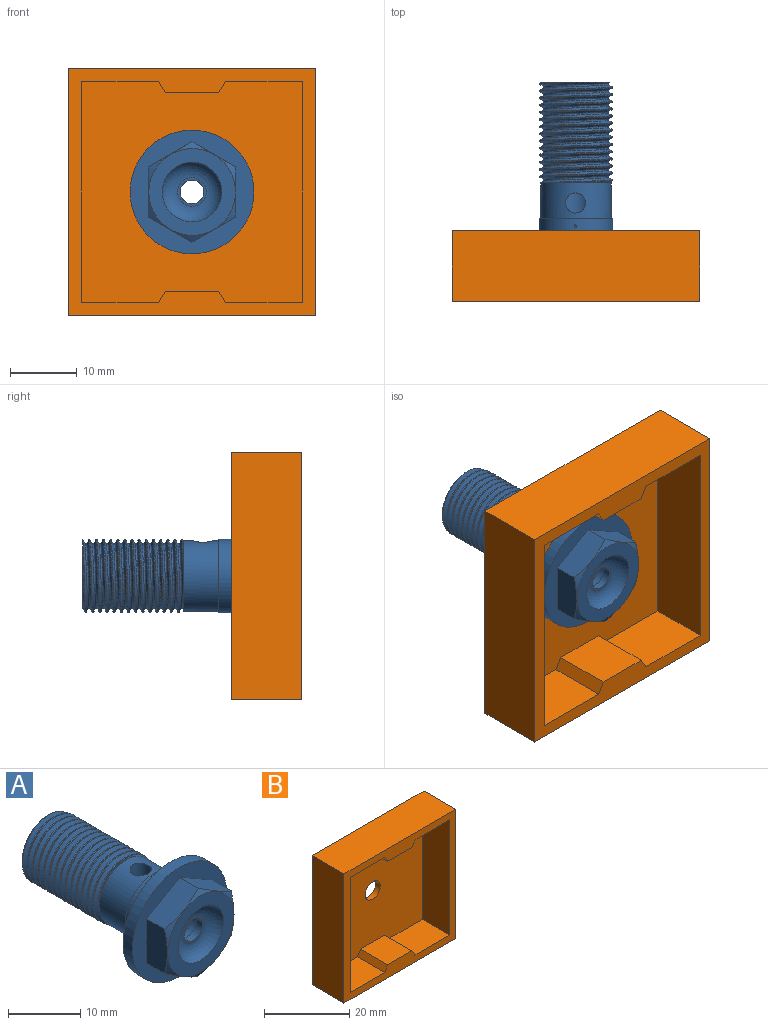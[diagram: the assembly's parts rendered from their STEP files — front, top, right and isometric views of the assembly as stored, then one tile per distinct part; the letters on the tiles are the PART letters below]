
ASSEMBLY  parts=2 mates=1
PART A: 32 faces, bbox 19.1x30.7x19.1 mm
  f0: cylinder r=2.36mm len=23.62mm, axis (0,1,0), area 343mm2, adj f15,f19,f20,f27
  f1: cylinder r=5.5mm len=11mm, axis (0,1,0), area 115.7mm2, adj f16,f18,f27
  f2: plane 12.96x12.96mm, normal (0,-1,0), area 69.8mm2, adj f25,f26
  f3: plane 6.5x4.11mm, normal (0.5,0,-0.87), area 29.3mm2, adj f4,f8,f12,f26
  f4: plane 8.13x4.74mm, normal (1,0,0), area 29.4mm2, adj f3,f5,f12,f26
  f5: plane 6.5x4.11mm, normal (0.5,0,0.87), area 29.3mm2, adj f4,f6,f12,f26
  f6: plane 6.5x4.1mm, normal (-0.5,0,0.87), area 29.2mm2, adj f5,f7,f12,f26
  f7: plane 7.51x4.09mm, normal (-1,0,0), area 29.2mm2, adj f6,f8,f12,f26
  f8: plane 6.5x4.1mm, normal (-0.5,0,-0.87), area 29.2mm2, adj f3,f7,f12,f26
  f9: cylinder r=1.79mm len=3.58mm, axis (0,1,0), area 13.4mm2, adj f22,f24
  f10: cylinder r=1.79mm len=3.58mm, axis (0,1,0), area 20.9mm2, adj f19,f23
  f11: cylinder r=5.25mm len=10.49mm, axis (0,1,0), area 168.6mm2, adj f14,f16,f20,f31
  f12: plane 18.49x18.49mm, normal (0,-1,0), area 122.2mm2, adj f3,f4,f5,f6,f7,f8,f17
  f13: cylinder r=5.46mm len=15.01mm, axis (0,1,0), area 82mm2, adj f14,f15,f29,f30
  f14: plane 7.42x6.99mm, normal (0,-1,0), area 1.7mm2, adj f11,f13,f29,f30
  f15: plane 10.6x10.55mm, normal (0,1,0), area 65.2mm2, adj f0,f13,f28,f29,f30
  f16: plane 11x11mm, normal (0,1,0), area 8.6mm2, adj f1,f11
  f17: cylinder r=9.25mm len=18.49mm, axis (0,1,0), area 106.2mm2, adj f12,f18
  f18: plane 18.49x18.49mm, normal (0,1,0), area 173.5mm2, adj f1,f17
  f19: plane 4.72x4.72mm, normal (0,1,0), area 7.5mm2, adj f0,f10
  f20: cylinder r=1.5mm len=3mm, axis (0,0,-1), area 27.2mm2, adj f0,f11
  f21: cylinder r=2.5mm len=5mm, axis (0,1,0), area 23.5mm2, adj f22,f23
  f22: plane 5x5mm, normal (0,1,0), area 9.6mm2, adj f9,f21
  f23: plane 5x5mm, normal (0,-1,0), area 9.6mm2, adj f10,f21
  f24: plane 4.28x4.28mm, normal (0,-1,0), area 4.3mm2, adj f9,f25
  f25: torus R=2.14mm, axis (0,1,0), area 62.4mm2, adj f2,f24
  f26: cone r=6.48mm half-angle=60deg, axis (0,1,0), area 18.3mm2, adj f2,f3,f4,f5,f6,f7,f8
  f27: cylinder r=0.19mm len=3.14mm, axis (0,0,-1), area 3.8mm2, adj f0,f1
  f28: bspline ~15.74x11.28mm, area 128.2mm2, adj f15,f29,f30,f31
  f29: bspline ~15.98x12.61mm, area 305.7mm2, adj f13,f14,f15,f28,f31
  f30: bspline ~15.8x12.61mm, area 304.6mm2, adj f13,f14,f15,f28,f31
  f31: plane 10.45x10.28mm, normal (0,1,0), area 5.5mm2, adj f11,f28,f29,f30
PART B: 20 faces, bbox 37x10.5x37 mm
  f0: plane 11.5x9mm, normal (0,0,1), area 103.5mm2, adj f2,f10,f11,f17
  f1: plane 11.5x9mm, normal (0,0,-1), area 103.5mm2, adj f2,f10,f11,f15
  f2: plane 33x33mm, normal (0,-1,0), area 1038.7mm2, adj f0,f1,f3,f4,f5,f10,f13,f14
  f3: plane 11.5x9mm, normal (0,0,1), area 103.5mm2, adj f2,f4,f11,f16
  f4: plane 33x9mm, normal (1,0,0), area 297mm2, adj f2,f3,f5,f11
  f5: plane 11.5x9mm, normal (0,0,-1), area 103.5mm2, adj f2,f4,f11,f13
  f6: plane 37x10.5mm, normal (-1,0,0), area 388.5mm2, adj f7,f9,f11,f12
  f7: plane 37x10.5mm, normal (0,0,-1), area 388.5mm2, adj f6,f8,f11,f12
  f8: plane 37x10.5mm, normal (1,0,0), area 388.5mm2, adj f7,f9,f11,f12
  f9: plane 37x10.5mm, normal (0,0,1), area 388.5mm2, adj f6,f8,f11,f12
  f10: plane 33x9mm, normal (-1,0,0), area 297mm2, adj f0,f1,f2,f11
  f11: plane 37x37mm, normal (0,-1,0), area 310.7mm2, adj f0,f1,f3,f4,f5,f6,f7,f8
  f12: plane 37x37mm, normal (0,1,0), area 1349.4mm2, adj f6,f7,f8,f9,f19
  f13: plane 9x1.71mm, normal (-0.86,0,-0.51), area 17.8mm2, adj f2,f5,f11,f14
  f14: plane 9x8mm, normal (0,0,-1), area 72mm2, adj f2,f11,f13,f15
  f15: plane 9x1.71mm, normal (0.86,0,-0.51), area 17.8mm2, adj f1,f2,f11,f14
  f16: plane 9x1.71mm, normal (-0.86,0,0.51), area 17.8mm2, adj f2,f3,f11,f18
  f17: plane 9x1.71mm, normal (0.86,0,0.51), area 17.8mm2, adj f0,f2,f11,f18
  f18: plane 9x8mm, normal (0,0,1), area 72mm2, adj f2,f11,f16,f17
  f19: cylinder r=2.5mm len=5mm, axis (0,-1,0), area 23.6mm2, adj f2,f12
PLACE A t=(18.5,20.14,18.5)mm
PLACE B at identity fixed
MATE revolute A.f0 <-> B.f19  axis (0,1,0) through (18.5,0,18.5)mm
